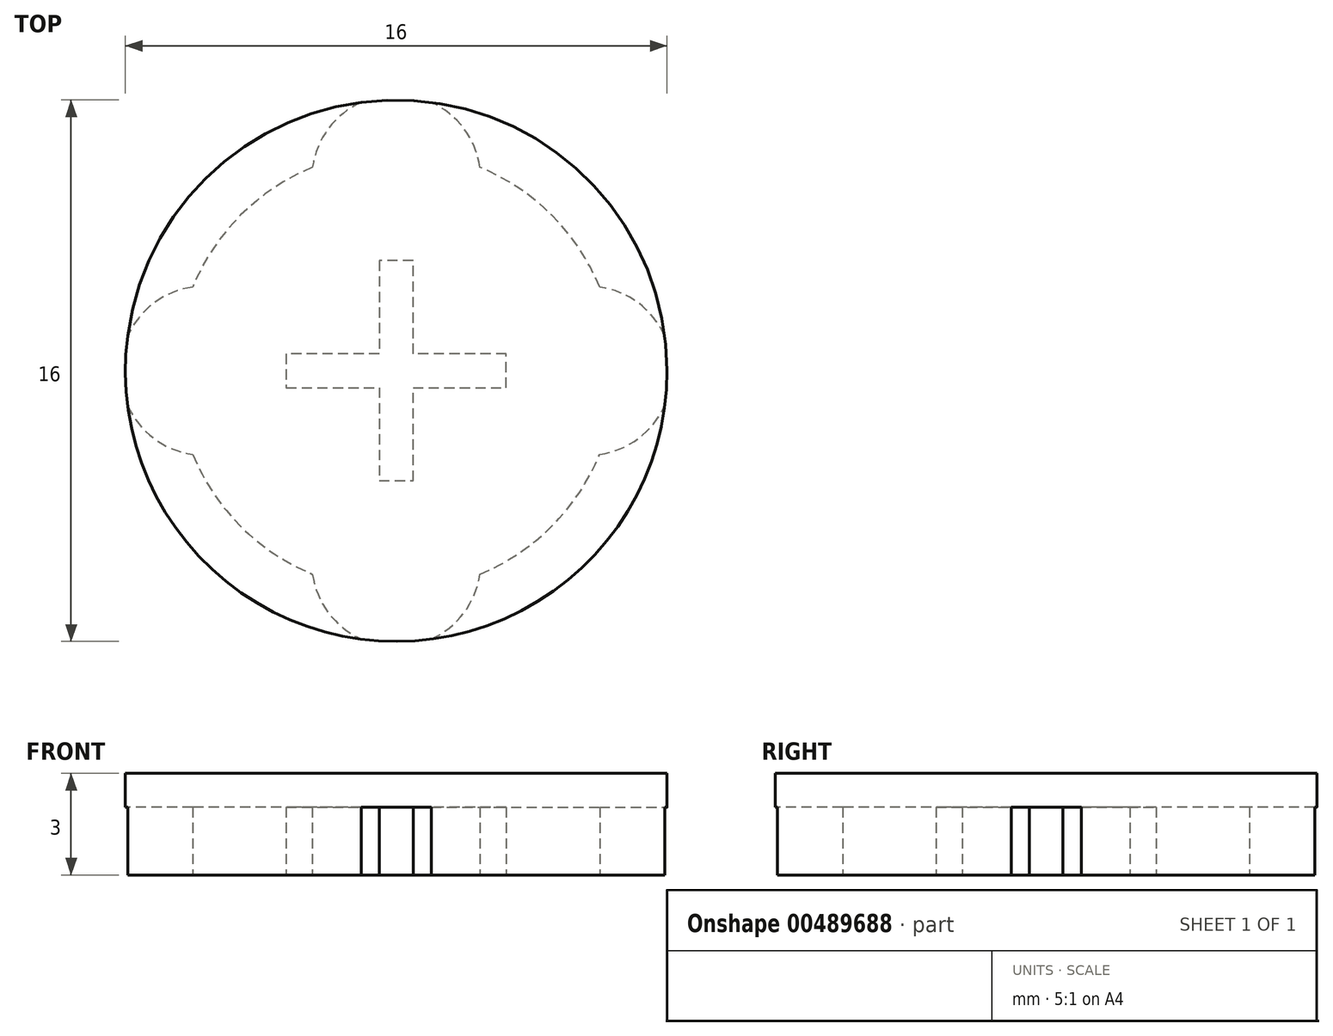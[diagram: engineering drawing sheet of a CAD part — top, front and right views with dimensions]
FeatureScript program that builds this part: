
annotation { "Feature Type Name" : "Feature", "Feature Type Description" : "" }
export const myFeature = defineFeature(function(context is Context, id is Id, definition is map)
    precondition{}
    {
        {
            var Q0;
            Q0=qCreatedBy(makeId("Top.planeOp"),FACE);
            var sketch = newSketch(context, id + "F0", { "sketchPlane" : qUnion([Q0])});
            skCircle(sketch, "E0", {"center": v(0, 0) * mm, "radius": 8 * mm});
            skSolve(sketch);
        }
        {
            var Q0;
            Q0=qSketchRegion(id+"F0",true);
            extrude(context, id + "F1", {"entities" : qUnion([Q0]), "depth" : 3 * mm});
        }
        {
            var Q0;
            Q0=makeQuery(id+"F1.opExtrude","CAP_FACE",FACE,{"disambiguationData":[OSD([sQuery(id+"F0.wireOp",EDGE,"E0")])],"isStart":true});
            var sketch = newSketch(context, id + "F2", { "sketchPlane" : qUnion([Q0])});
            skArc(sketch, "E1", {"start": v(-6.01, -2.47) * mm, "mid": v(-4.6, -4.6) * mm, "end": v(-2.47, -6.01) * mm});
            skLineSegment(sketch, "E2", {"start": v(-0.5, 3.25) * mm, "end": v(0.5, 3.25) * mm});
            skLineSegment(sketch, "E3", {"start": v(0.5, 3.25) * mm, "end": v(0.5, 0.5) * mm});
            skLineSegment(sketch, "E4", {"start": v(0.5, 0.5) * mm, "end": v(3.25, 0.5) * mm});
            skLineSegment(sketch, "E5", {"start": v(3.25, 0.5) * mm, "end": v(3.25, -0.5) * mm});
            skLineSegment(sketch, "E6", {"start": v(3.25, -0.5) * mm, "end": v(0.5, -0.5) * mm});
            skLineSegment(sketch, "E7", {"start": v(0.5, -0.5) * mm, "end": v(0.5, -3.25) * mm});
            skLineSegment(sketch, "E8", {"start": v(0.5, -3.25) * mm, "end": v(-0.5, -3.25) * mm});
            skLineSegment(sketch, "E9", {"start": v(-0.5, -3.25) * mm, "end": v(-0.5, -0.5) * mm});
            skLineSegment(sketch, "E10", {"start": v(-0.5, -0.5) * mm, "end": v(-3.25, -0.5) * mm});
            skLineSegment(sketch, "E11", {"start": v(-3.25, -0.5) * mm, "end": v(-3.25, 0.5) * mm});
            skLineSegment(sketch, "E12", {"start": v(-3.25, 0.5) * mm, "end": v(-0.5, 0.5) * mm});
            skLineSegment(sketch, "E13", {"start": v(-0.5, 0.5) * mm, "end": v(-0.5, 3.25) * mm});
            skLineSegment(sketch, "E14", {"start": v(0, 5.66) * mm, "end": v(0, -5.66) * mm, "construction": true});
            skLineSegment(sketch, "E15", {"start": v(-5.66, 0) * mm, "end": v(5.66, 0) * mm, "construction": true});
            skPoint(sketch, "E15.startSnap0", {"position": v(-3.25, 0) * mm});
            skArc(sketch, "E16", {"start": v(-7.93, -1.03) * mm, "mid": v(-7.16, -2) * mm, "end": v(-6.01, -2.47) * mm});
            skArc(sketch, "E17", {"start": v(7.93, 1.03) * mm, "mid": v(7.16, 2) * mm, "end": v(6.01, 2.47) * mm});
            skArc(sketch, "E18", {"start": v(-1.03, 7.93) * mm, "mid": v(-2, 7.16) * mm, "end": v(-2.47, 6.01) * mm});
            skArc(sketch, "E19", {"start": v(1.03, -7.93) * mm, "mid": v(2, -7.16) * mm, "end": v(2.47, -6.01) * mm});
            skPoint(sketch, "E20.orphan", {"position": v(-8.95, 0) * mm});
            skPoint(sketch, "E21.orphan", {"position": v(0, 9.07) * mm});
            skArc(sketch, "E22", {"start": v(-7.93, 1.03) * mm, "mid": v(-8, 0) * mm, "end": v(-7.93, -1.03) * mm});
            skArc(sketch, "E23.trimOffspring", {"start": v(-2.47, 6.01) * mm, "mid": v(-4.6, 4.6) * mm, "end": v(-6.01, 2.47) * mm});
            skArc(sketch, "E24.trimOffspring", {"start": v(1.03, 7.93) * mm, "mid": v(0, 8) * mm, "end": v(-1.03, 7.93) * mm});
            skArc(sketch, "E25.trimOffspring", {"start": v(7.93, -1.03) * mm, "mid": v(8, 0) * mm, "end": v(7.93, 1.03) * mm});
            skArc(sketch, "E26.trimOffspring", {"start": v(-1.03, -7.93) * mm, "mid": v(0, -8) * mm, "end": v(1.03, -7.93) * mm});
            skArc(sketch, "E27.trimOffspring", {"start": v(2.47, -6.01) * mm, "mid": v(4.6, -4.6) * mm, "end": v(6.01, -2.47) * mm});
            skArc(sketch, "E28.trimOffspring", {"start": v(6.01, 2.47) * mm, "mid": v(4.6, 4.6) * mm, "end": v(2.47, 6.01) * mm});
            skArc(sketch, "E29.trimOffspring", {"start": v(6.01, -2.47) * mm, "mid": v(7.16, -2) * mm, "end": v(7.93, -1.03) * mm});
            skArc(sketch, "E30.trimOffspring", {"start": v(2.47, 6.01) * mm, "mid": v(2, 7.16) * mm, "end": v(1.03, 7.93) * mm});
            skArc(sketch, "E31.trimOffspring", {"start": v(-6.01, 2.47) * mm, "mid": v(-7.16, 2) * mm, "end": v(-7.93, 1.03) * mm});
            skArc(sketch, "E32.trimOffspring", {"start": v(-2.47, -6.01) * mm, "mid": v(-2, -7.16) * mm, "end": v(-1.03, -7.93) * mm});
            skSolve(sketch);
        }
        {
            var Q0;
            Q0=makeQuery(id+"F2.imprint","IMPRINT",FACE,{"disambiguationData":[TD([[makeQuery(id+"F2.imprint","IMPRINT",EDGE,{"derivedFrom":sQuery(id+"F2.wireOp",EDGE,"E1")}),1.0]])]});
            extrude(context, id + "F3", {"entities" : qUnion([Q0]), "operationType" : NewBodyOperationType.REMOVE, "oppositeDirection" : true, "depth" : 2 * mm});
        }
    });
